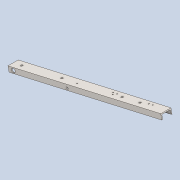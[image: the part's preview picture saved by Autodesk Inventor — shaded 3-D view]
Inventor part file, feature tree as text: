
AUTODESK INVENTOR PART (.ipt)
format: ipt  version: 2021 (Build 250183000, 183)  size: 133,120 bytes
history: native  units: mm
features: other x1, extrude x1, sketch x1, imported_body x1
ambient origin geometry x8: Origin, YZ Plane, XZ Plane, XY Plane, X Axis, Y Axis, Z Axis, Center Point
bodies: Body1 (feature_tree)
feature tree (4):
  other  "Sólido1"
  extrude  "Extrusión1"  TaperAngle=0.0deg  [1 undecoded]
  sketch  "Boceto1"  dims[d0=19.0mm d1=0.0mm d2=0.0mm d3=24.469027mm]
  imported_body  "Base1"
note: 1 required parameter value undecoded (feature->parameter linkage not recoverable at this tier; creation-order binding heuristic only, values carry confidence <= 0.55)
